# Revit family: Table-Teknion-CHPH-Chronicle-Height_Adjustable_Double_Pedestal_desk-Full_Modesty-R2022
name_source: partatom
category: Furniture
units: mm (PartAtom-declared; Revit-internal decimal feet)

## family parameters
Always vertical = Yes
Cut with Voids When Loaded = No
OmniClass Number = 23.40.20.00
OmniClass Title = General Furniture and Specialties
Render Appearance Source = Family Geometry
Room Calculation Point = No
Shared = Yes
Work Plane-Based = No

## types (6) — shared parameters
Assembly Code = E2020200
Height = 29 "
Left/Right Hinged = Yes
Manufacturer = Teknion
Manufacturer Fax = 416.661.4586
Part Number = CHPH
Product Line = Height adjustable Double Pedestal Desk
Product Page URL = https://www.teknion.com
Series = Chronicle
Sustainability Data = https://www.teknion.com
URL = www.teknion.com
Unit Weight URL = http://www.teknion.com
Warranty = http://www.teknion.com
zero-valued in all types: Default Elevation

## per-type parameters (varying)
| type | (B)Left/Right 2 Box, 1 File | (F)Left/Right, 2 File | (G)Left 2 Box 1 File, Right Hinged Door | (H)Left Hinged Door, Right 2 Box 1 File | (R)Left 2 File, Right 2 Box 1 File | Description | Model |
| (H) Left Hinged Door, Right 2 Box 1 File | No | No | No | Yes | No | HA Desk - Left Hinged Door, Right 2 Box 1 File | CHPH_____BH_ |
| (G) Left 2 Box 1 File, Right Hinged Door | No | No | Yes | No | No | HA Desk - Left 2 Box 1 File, Right Hinged Door | CHPH_____BG_ |
| (L)Left 2 Box 1 File, Right 2 File | No | No | No | No | No | HA Desk - Left 2 Box 1 File, Right 2 File | CHPH_____BL_ |
| (R) Left 2 File, Right 2 Box 1 File | No | No | No | No | Yes | HA Desk - Left 2 File, Right 2 Box 1 File | CHPH_____BR_ |
| (B) Left/Right 2 Box, 1 File | Yes | No | No | No | No | HA Desk - Both Sides 2 Box,1 File | CHPH_____BB_ |
| (F) Left/Right, 2 File | No | Yes | No | No | No | HA Desk - Both Sides 2 File | CHPH_____BF_ |

type visibility flags (boolean, named after types; folded from table):
- (H) Left Hinged Door, Right 2 Box 1 File: Yes: (none)
- (G) Left 2 Box 1 File, Right Hinged Door: Yes: (none)
- (L)Left 2 Box 1 File, Right 2 File: Yes: (L)Left 2 Box 1 File, Right 2 File
- (R) Left 2 File, Right 2 Box 1 File: Yes: (none)
- (B) Left/Right 2 Box, 1 File: Yes: (none)
- (F) Left/Right, 2 File: Yes: (none)

## geometry (parser evidence)
native form markers: Sweep x5
no freeform markers — native parametric forms only
